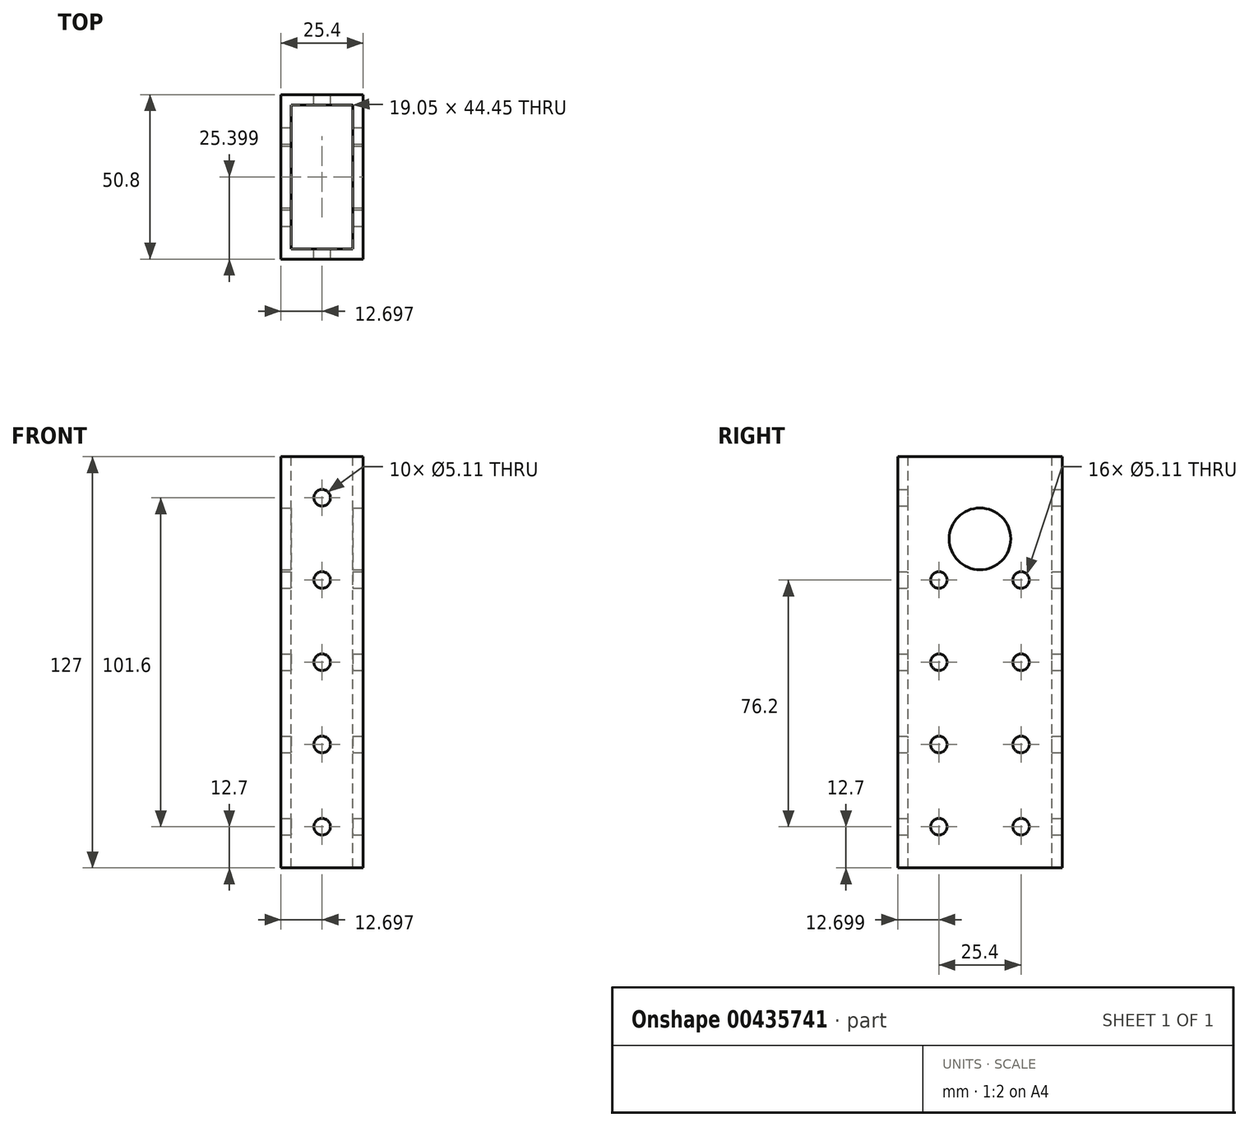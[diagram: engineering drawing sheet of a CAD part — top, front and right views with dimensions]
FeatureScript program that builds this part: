
annotation { "Feature Type Name" : "Feature", "Feature Type Description" : "" }
export const myFeature = defineFeature(function(context is Context, id is Id, definition is map)
    precondition{}
    {
        {
            var Q0;
            Q0=qCreatedBy(makeId("Top.planeOp"),FACE);
            var sketch = newSketch(context, id + "F0", { "sketchPlane" : qUnion([Q0])});
            skLineSegment(sketch, "E0.bottom", {"start": v(-14.42, 31.7) * mm, "end": v(10.98, 31.7) * mm});
            skLineSegment(sketch, "E0.top", {"start": v(-14.42, -19.1) * mm, "end": v(10.98, -19.1) * mm});
            skLineSegment(sketch, "E0.left", {"start": v(-14.42, 31.7) * mm, "end": v(-14.42, -19.1) * mm});
            skLineSegment(sketch, "E0.right", {"start": v(10.98, 31.7) * mm, "end": v(10.98, -19.1) * mm});
            skSolve(sketch);
        }
        {
            var Q0;
            Q0=makeQuery(id+"F0.imprint","IMPRINT",FACE,{"disambiguationData":[TD([[makeQuery(id+"F0.imprint","IMPRINT",EDGE,{"derivedFrom":sQuery(id+"F0.wireOp",EDGE,"E0.bottom")}),-1.0]])]});
            extrude(context, id + "F1", {"entities" : qUnion([Q0]), "depth" : 127 * mm});
        }
        {
            var Q0;
            Q0=makeQuery(id+"F1.opExtrude","CAP_FACE",FACE,{"disambiguationData":[OSD([sQuery(id+"F0.wireOp",EDGE,"E0.bottom"),sQuery(id+"F0.wireOp",EDGE,"E0.top"),sQuery(id+"F0.wireOp",EDGE,"E0.left"),sQuery(id+"F0.wireOp",EDGE,"E0.right")])],"isStart":false});
            var sketch = newSketch(context, id + "F2", { "sketchPlane" : qUnion([Q0])});
            skLineSegment(sketch, "E1.bottom", {"start": v(-11.25, 28.53) * mm, "end": v(7.8, 28.53) * mm});
            skLineSegment(sketch, "E1.top", {"start": v(-11.25, -15.92) * mm, "end": v(7.8, -15.92) * mm});
            skLineSegment(sketch, "E1.left", {"start": v(-11.25, 28.53) * mm, "end": v(-11.25, -15.92) * mm});
            skLineSegment(sketch, "E1.right", {"start": v(7.8, 28.53) * mm, "end": v(7.8, -15.92) * mm});
            skSolve(sketch);
        }
        {
            var Q0;
            Q0=makeQuery(id+"F2.imprint","IMPRINT",FACE,{"disambiguationData":[TD([[makeQuery(id+"F2.imprint","IMPRINT",EDGE,{"derivedFrom":sQuery(id+"F2.wireOp",EDGE,"E1.bottom")}),-1.0]])]});
            extrude(context, id + "F3", {"entities" : qUnion([Q0]), "operationType" : NewBodyOperationType.REMOVE, "oppositeDirection" : true, "depth" : 127 * mm});
        }
        {
            var Q0;
            Q0=makeQuery(id+"F1.opExtrude","SWEPT_FACE",FACE,{"disambiguationData":[OSD([sQuery(id+"F0.wireOp",EDGE,"E0.right")])]});
            var sketch = newSketch(context, id + "F4", { "sketchPlane" : qUnion([Q0])});
            skCircle(sketch, "E2", {"center": v(6.3, 101.6) * mm, "radius": 9.53 * mm});
            skCircle(sketch, "E3", {"center": v(-6.4, 12.7) * mm, "radius": 2.55 * mm});
            skCircle(sketch, "E4.0.1.0", {"center": v(-6.4, 38.1) * mm, "radius": 2.55 * mm});
            skCircle(sketch, "E4.0.2.0", {"center": v(-6.4, 63.5) * mm, "radius": 2.55 * mm});
            skCircle(sketch, "E4.0.3.0", {"center": v(-6.4, 88.9) * mm, "radius": 2.55 * mm});
            skCircle(sketch, "E4.1.0.0", {"center": v(19, 12.7) * mm, "radius": 2.55 * mm});
            skCircle(sketch, "E4.1.1.0", {"center": v(19, 38.1) * mm, "radius": 2.55 * mm});
            skCircle(sketch, "E4.1.2.0", {"center": v(19, 63.5) * mm, "radius": 2.55 * mm});
            skCircle(sketch, "E4.1.3.0", {"center": v(19, 88.9) * mm, "radius": 2.55 * mm});
            skLineSegment(sketch, "E4.direction1", {"start": v(-6.4, 12.7) * mm, "end": v(19, 12.7) * mm, "construction": true});
            skLineSegment(sketch, "E4.direction2", {"start": v(-6.4, 12.7) * mm, "end": v(-6.4, 38.1) * mm, "construction": true});
            skSolve(sketch);
        }
        {
            var Q0;
            Q0=sQuery(id+"F4.wireOp",VERTEX,"E2.center");
            var Q1;
            Q1=makeQuery(id+"F1.opExtrude","SWEPT_BODY",BODY,{"disambiguationData":[OSD([sQuery(id+"F0.wireOp",EDGE,"E0.bottom"),sQuery(id+"F0.wireOp",EDGE,"E0.top"),sQuery(id+"F0.wireOp",EDGE,"E0.left"),sQuery(id+"F0.wireOp",EDGE,"E0.right")])]});
            hole(context, id + "F5", {"style" : HoleStyle.SIMPLE, "endStyle" : HoleEndStyle.THROUGH, "holeDiameter" : 19.05 * mm, "isTappedThrough" : true, "tappedDepth" : 12.7 * mm, "tapClearance" : 3, "locations" : qUnion([Q0]), "scope" : qUnion([Q1])});
        }
        {
            var Q0;
            Q0=sQuery(id+"F4.wireOp",VERTEX,"E4.0.2.0.center");
            var Q1;
            Q1=sQuery(id+"F4.wireOp",VERTEX,"E4.0.4.0.center");
            var Q2;
            Q2=sQuery(id+"F4.wireOp",VERTEX,"E4.0.3.0.center");
            var Q3;
            Q3=sQuery(id+"F4.wireOp",VERTEX,"E4.0.1.0.center");
            var Q4;
            Q4=sQuery(id+"F4.wireOp",VERTEX,"E3.center");
            var Q5;
            Q5=sQuery(id+"F4.wireOp",VERTEX,"E4.0.5.0.center");
            var Q6;
            Q6=sQuery(id+"F4.wireOp",VERTEX,"E4.1.1.0.center");
            var Q7;
            Q7=sQuery(id+"F4.wireOp",VERTEX,"E4.1.4.0.center");
            var Q8;
            Q8=sQuery(id+"F4.wireOp",VERTEX,"E4.1.0.0.center");
            var Q9;
            Q9=sQuery(id+"F4.wireOp",VERTEX,"E4.1.2.0.center");
            var Q10;
            Q10=sQuery(id+"F4.wireOp",VERTEX,"E4.1.3.0.center");
            var Q11;
            Q11=sQuery(id+"F4.wireOp",VERTEX,"E4.1.5.0.center");
            var Q12;
            Q12=makeQuery(id+"F1.opExtrude","SWEPT_BODY",BODY,{"disambiguationData":[OSD([sQuery(id+"F0.wireOp",EDGE,"E0.bottom"),sQuery(id+"F0.wireOp",EDGE,"E0.top"),sQuery(id+"F0.wireOp",EDGE,"E0.left"),sQuery(id+"F0.wireOp",EDGE,"E0.right")])]});
            hole(context, id + "F6", {"style" : HoleStyle.SIMPLE, "endStyle" : HoleEndStyle.THROUGH, "holeDiameter" : 5.1 * mm, "isTappedThrough" : true, "tappedDepth" : 12.7 * mm, "tapClearance" : 3, "locations" : qUnion([Q0, Q1, Q2, Q3, Q4, Q5, Q6, Q7, Q8, Q9, Q10, Q11]), "scope" : qUnion([Q12])});
        }
        {
            var Q0;
            Q0=makeQuery(id+"F1.opExtrude","SWEPT_FACE",FACE,{"disambiguationData":[OSD([sQuery(id+"F0.wireOp",EDGE,"E0.bottom")])]});
            var sketch = newSketch(context, id + "F7", { "sketchPlane" : qUnion([Q0])});
            skCircle(sketch, "E5", {"center": v(1.72, 12.7) * mm, "radius": 2.55 * mm});
            skPoint(sketch, "E5.centerSnap0", {"position": v(1.72, 0) * mm});
            skCircle(sketch, "E6.0.1.0", {"center": v(1.72, 38.1) * mm, "radius": 2.55 * mm});
            skCircle(sketch, "E6.0.2.0", {"center": v(1.72, 63.5) * mm, "radius": 2.55 * mm});
            skCircle(sketch, "E6.0.3.0", {"center": v(1.72, 88.9) * mm, "radius": 2.55 * mm});
            skCircle(sketch, "E6.0.4.0", {"center": v(1.72, 114.3) * mm, "radius": 2.55 * mm});
            skLineSegment(sketch, "E6.direction1", {"start": v(1.72, 12.7) * mm, "end": v(27.12, 12.7) * mm, "construction": true});
            skLineSegment(sketch, "E6.direction2", {"start": v(1.72, 12.7) * mm, "end": v(1.72, 38.1) * mm, "construction": true});
            skSolve(sketch);
        }
        {
            var Q0;
            Q0=sQuery(id+"F7.wireOp",VERTEX,"E6.0.3.0.center");
            var Q1;
            Q1=sQuery(id+"F7.wireOp",VERTEX,"E6.0.2.0.center");
            var Q2;
            Q2=sQuery(id+"F7.wireOp",VERTEX,"E6.0.5.0.center");
            var Q3;
            Q3=sQuery(id+"F7.wireOp",VERTEX,"E6.0.4.0.center");
            var Q4;
            Q4=sQuery(id+"F7.wireOp",VERTEX,"E6.0.6.0.center");
            var Q5;
            Q5=sQuery(id+"F7.wireOp",VERTEX,"E5.center");
            var Q6;
            Q6=sQuery(id+"F7.wireOp",VERTEX,"E6.0.1.0.center");
            var Q7;
            Q7=makeQuery(id+"F1.opExtrude","SWEPT_BODY",BODY,{"disambiguationData":[OSD([sQuery(id+"F0.wireOp",EDGE,"E0.bottom"),sQuery(id+"F0.wireOp",EDGE,"E0.top"),sQuery(id+"F0.wireOp",EDGE,"E0.left"),sQuery(id+"F0.wireOp",EDGE,"E0.right")])]});
            hole(context, id + "F8", {"style" : HoleStyle.SIMPLE, "endStyle" : HoleEndStyle.THROUGH, "holeDiameter" : 5.1 * mm, "isTappedThrough" : true, "tappedDepth" : 12.7 * mm, "tapClearance" : 3, "locations" : qUnion([Q0, Q1, Q2, Q3, Q4, Q5, Q6]), "scope" : qUnion([Q7])});
        }
    });
